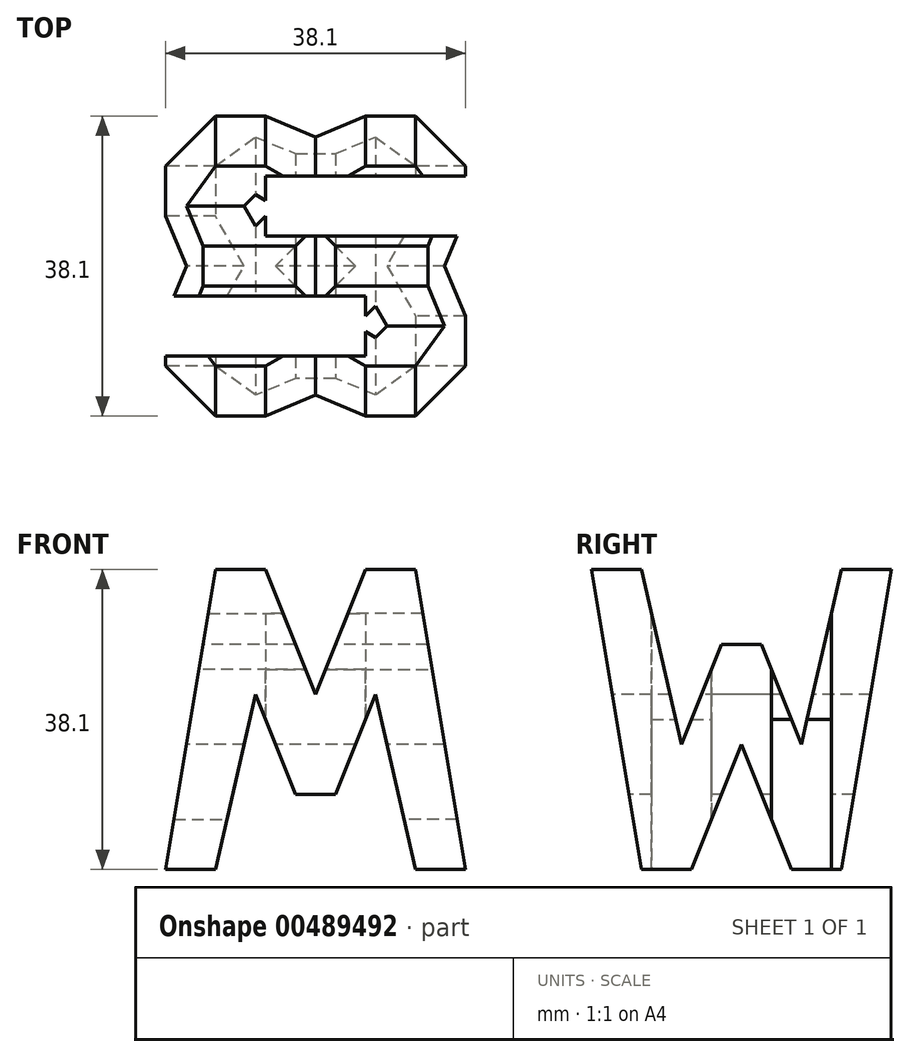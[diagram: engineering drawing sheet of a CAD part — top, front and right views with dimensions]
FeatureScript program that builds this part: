
annotation { "Feature Type Name" : "Feature", "Feature Type Description" : "" }
export const myFeature = defineFeature(function(context is Context, id is Id, definition is map)
    precondition{}
    {
        {
            var Q0;
            Q0=qCreatedBy(makeId("Front.planeOp"),FACE);
            var sketch = newSketch(context, id + "F0", { "sketchPlane" : qUnion([Q0])});
            skLineSegment(sketch, "E0", {"start": v(0, 0) * mm, "end": v(0, 38.1) * mm});
            skLineSegment(sketch, "E1", {"start": v(0, 38.1) * mm, "end": v(-38.1, 38.1) * mm});
            skLineSegment(sketch, "E2", {"start": v(-38.1, 38.1) * mm, "end": v(-38.1, 0) * mm});
            skLineSegment(sketch, "E3", {"start": v(-38.1, 0) * mm, "end": v(0, 0) * mm});
            skSolve(sketch);
        }
        {
            var Q0;
            Q0=makeQuery(id+"F0.imprint","IMPRINT",FACE,{"disambiguationData":[TD([[makeQuery(id+"F0.imprint","IMPRINT",EDGE,{"derivedFrom":sQuery(id+"F0.wireOp",EDGE,"E0")}),1.0]])]});
            extrude(context, id + "F1", {"entities" : qUnion([Q0]), "depth" : 38.1 * mm, "offsetDistance" : 25.4 * mm});
        }
        {
            var Q0;
            Q0=qCreatedBy(makeId("Front.planeOp"),FACE);
            cPlane(context, id + "F2", {"entities" : qUnion([Q0]), "cplaneType" : CPlaneType.OFFSET, "offset" : 38.1 * mm, "width" : 152.4 * mm, "height" : 152.4 * mm});
        }
        {
            var Q0;
            Q0=qCreatedBy(makeId("Right.planeOp"),FACE);
            cPlane(context, id + "F3", {"entities" : qUnion([Q0]), "cplaneType" : CPlaneType.OFFSET, "offset" : 38.1 * mm, "oppositeDirection" : true, "width" : 152.4 * mm, "height" : 152.4 * mm});
        }
        {
            var Q0;
            Q0=qCreatedBy(makeId("Top.planeOp"),FACE);
            cPlane(context, id + "F4", {"entities" : qUnion([Q0]), "cplaneType" : CPlaneType.OFFSET, "offset" : 38.1 * mm, "width" : 152.4 * mm, "height" : 152.4 * mm});
        }
        {
            var Q0;
            Q0=qCreatedBy(id+"F3.planeOp",FACE);
            var sketch = newSketch(context, id + "F5", { "sketchPlane" : qUnion([Q0])});
            skLineSegment(sketch, "E4", {"start": v(0, 38.1) * mm, "end": v(-38.1, 38.1) * mm});
            skLineSegment(sketch, "E5", {"start": v(-38.1, 38.1) * mm, "end": v(-38.1, 0) * mm});
            skLineSegment(sketch, "E6", {"start": v(0, 38.1) * mm, "end": v(-6.35, 0) * mm});
            skLineSegment(sketch, "E7", {"start": v(-6.35, 0) * mm, "end": v(-12.7, 0) * mm});
            skLineSegment(sketch, "E8", {"start": v(-12.7, 0) * mm, "end": v(-19.05, 15.88) * mm});
            skLineSegment(sketch, "E9", {"start": v(-19.05, 15.88) * mm, "end": v(-25.4, 0) * mm});
            skLineSegment(sketch, "E10", {"start": v(-25.4, 0) * mm, "end": v(-31.75, 0) * mm});
            skLineSegment(sketch, "E11", {"start": v(-31.75, 0) * mm, "end": v(-38.1, 38.1) * mm});
            skLineSegment(sketch, "E12", {"start": v(-31.75, 38.1) * mm, "end": v(-26.67, 15.88) * mm});
            skLineSegment(sketch, "E13", {"start": v(-26.67, 15.88) * mm, "end": v(-21.59, 28.58) * mm});
            skLineSegment(sketch, "E14", {"start": v(-21.6, 28.58) * mm, "end": v(-16.51, 28.58) * mm});
            skLineSegment(sketch, "E15", {"start": v(-16.51, 28.58) * mm, "end": v(-11.43, 15.88) * mm});
            skLineSegment(sketch, "E16", {"start": v(-11.43, 15.88) * mm, "end": v(-6.35, 38.1) * mm});
            skLineSegment(sketch, "E17", {"start": v(-6.35, 38.1) * mm, "end": v(0, 38.1) * mm});
            skLineSegment(sketch, "E18", {"start": v(0, 38.1) * mm, "end": v(0, 0) * mm});
            skLineSegment(sketch, "E19", {"start": v(0, 0) * mm, "end": v(-38.1, 0) * mm});
            skSolve(sketch);
        }
        {
            var Q0;
            {var subQ0=sQuery(id+"F5.wireOp",EDGE,"E12");Q0=makeQuery(id+"F5.imprint","IMPRINT",FACE,{"disambiguationData":[TD([[makeQuery(id+"F5.imprint","IMPRINT",EDGE,{"derivedFrom":subQ0}),1.0]])]});}
            var Q1;
            {var subQ0=sQuery(id+"F5.wireOp",EDGE,"E6");Q1=makeQuery(id+"F5.imprint","IMPRINT",FACE,{"disambiguationData":[TD([[makeQuery(id+"F5.imprint","IMPRINT",EDGE,{"derivedFrom":subQ0}),1.0]])]});}
            var Q2;
            {var subQ0=sQuery(id+"F5.wireOp",EDGE,"E8");Q2=makeQuery(id+"F5.imprint","IMPRINT",FACE,{"disambiguationData":[TD([[makeQuery(id+"F5.imprint","IMPRINT",EDGE,{"derivedFrom":subQ0}),1.0]])]});}
            var Q3;
            {var subQ0=sQuery(id+"F5.wireOp",EDGE,"E5");Q3=makeQuery(id+"F5.imprint","IMPRINT",FACE,{"disambiguationData":[TD([[makeQuery(id+"F5.imprint","IMPRINT",EDGE,{"derivedFrom":subQ0}),1.0]])]});}
            extrude(context, id + "F6", {"entities" : qUnion([Q0, Q1, Q2, Q3]), "operationType" : NewBodyOperationType.REMOVE, "depth" : 38.1 * mm, "offsetDistance" : 25.4 * mm});
        }
        {
            var Q0;
            Q0=qCreatedBy(id+"F2.planeOp",FACE);
            var sketch = newSketch(context, id + "F7", { "sketchPlane" : qUnion([Q0])});
            skLineSegment(sketch, "E20", {"start": v(-38.1, 38.1) * mm, "end": v(0, 38.1) * mm});
            skLineSegment(sketch, "E21", {"start": v(0, 38.1) * mm, "end": v(0, 0) * mm});
            skLineSegment(sketch, "E22", {"start": v(0, 0) * mm, "end": v(-38.1, 0) * mm});
            skLineSegment(sketch, "E23", {"start": v(-38.1, 0) * mm, "end": v(-38.1, 38.1) * mm});
            skLineSegment(sketch, "E24", {"start": v(-38.1, 0) * mm, "end": v(-31.75, 38.1) * mm});
            skLineSegment(sketch, "E25", {"start": v(-31.75, 38.1) * mm, "end": v(-25.4, 38.1) * mm});
            skLineSegment(sketch, "E26", {"start": v(-25.4, 38.1) * mm, "end": v(-19.05, 22.22) * mm});
            skLineSegment(sketch, "E27", {"start": v(-19.05, 22.22) * mm, "end": v(-12.7, 38.1) * mm});
            skLineSegment(sketch, "E28", {"start": v(-12.7, 38.1) * mm, "end": v(-6.35, 38.1) * mm});
            skLineSegment(sketch, "E29", {"start": v(-6.35, 38.1) * mm, "end": v(0, 0) * mm});
            skLineSegment(sketch, "E30", {"start": v(-6.35, 0) * mm, "end": v(-11.43, 22.22) * mm});
            skLineSegment(sketch, "E31", {"start": v(-11.43, 22.22) * mm, "end": v(-16.5, 9.52) * mm});
            skLineSegment(sketch, "E32", {"start": v(-16.5, 9.52) * mm, "end": v(-21.59, 9.52) * mm});
            skLineSegment(sketch, "E33", {"start": v(-21.59, 9.52) * mm, "end": v(-26.67, 22.22) * mm});
            skLineSegment(sketch, "E34", {"start": v(-26.67, 22.22) * mm, "end": v(-31.75, 0) * mm});
            skLineSegment(sketch, "E35", {"start": v(-31.75, 0) * mm, "end": v(-38.1, 0) * mm});
            skSolve(sketch);
        }
        {
            var Q0;
            {var subQ0=sQuery(id+"F7.wireOp",EDGE,"E30");Q0=makeQuery(id+"F7.imprint","IMPRINT",FACE,{"disambiguationData":[TD([[makeQuery(id+"F7.imprint","IMPRINT",EDGE,{"derivedFrom":subQ0}),1.0]])]});}
            var Q1;
            {var subQ0=sQuery(id+"F7.wireOp",EDGE,"E23");Q1=makeQuery(id+"F7.imprint","IMPRINT",FACE,{"disambiguationData":[TD([[makeQuery(id+"F7.imprint","IMPRINT",EDGE,{"derivedFrom":subQ0}),-1.0]])]});}
            var Q2;
            {var subQ0=sQuery(id+"F7.wireOp",EDGE,"E26");Q2=makeQuery(id+"F7.imprint","IMPRINT",FACE,{"disambiguationData":[TD([[makeQuery(id+"F7.imprint","IMPRINT",EDGE,{"derivedFrom":subQ0}),1.0]])]});}
            var Q3;
            {var subQ0=sQuery(id+"F7.wireOp",EDGE,"E21");Q3=makeQuery(id+"F7.imprint","IMPRINT",FACE,{"disambiguationData":[TD([[makeQuery(id+"F7.imprint","IMPRINT",EDGE,{"derivedFrom":subQ0}),-1.0]])]});}
            extrude(context, id + "F8", {"entities" : qUnion([Q0, Q1, Q2, Q3]), "operationType" : NewBodyOperationType.REMOVE, "oppositeDirection" : true, "depth" : 38.1 * mm, "offsetDistance" : 25.4 * mm});
        }
        {
            var Q0;
            Q0=qCreatedBy(id+"F4.planeOp",FACE);
            var sketch = newSketch(context, id + "F9", { "sketchPlane" : qUnion([Q0])});
            skLineSegment(sketch, "E36", {"start": v(0, 0) * mm, "end": v(0, -38.1) * mm});
            skLineSegment(sketch, "E37", {"start": v(0, -38.1) * mm, "end": v(-38.1, -38.1) * mm});
            skLineSegment(sketch, "E38", {"start": v(-38.1, -38.1) * mm, "end": v(-38.1, 0) * mm});
            skLineSegment(sketch, "E39", {"start": v(-38.1, 0) * mm, "end": v(0, 0) * mm});
            skLineSegment(sketch, "E40", {"start": v(0, -7.62) * mm, "end": v(-25.4, -7.62) * mm});
            skLineSegment(sketch, "E41", {"start": v(-25.4, -7.62) * mm, "end": v(-25.4, -15.24) * mm});
            skLineSegment(sketch, "E42", {"start": v(-25.4, -15.24) * mm, "end": v(0, -15.24) * mm});
            skLineSegment(sketch, "E43", {"start": v(-38.1, -30.48) * mm, "end": v(-12.7, -30.48) * mm});
            skLineSegment(sketch, "E44", {"start": v(-12.7, -30.48) * mm, "end": v(-12.7, -22.86) * mm});
            skLineSegment(sketch, "E45", {"start": v(-12.7, -22.86) * mm, "end": v(-38.1, -22.86) * mm});
            skSolve(sketch);
        }
        {
            var Q0;
            {var subQ0=sQuery(id+"F9.wireOp",EDGE,"E40");Q0=makeQuery(id+"F9.imprint","IMPRINT",FACE,{"disambiguationData":[TD([[makeQuery(id+"F9.imprint","IMPRINT",EDGE,{"derivedFrom":subQ0}),1.0]])]});}
            var Q1;
            {var subQ0=sQuery(id+"F9.wireOp",EDGE,"E43");Q1=makeQuery(id+"F9.imprint","IMPRINT",FACE,{"disambiguationData":[TD([[makeQuery(id+"F9.imprint","IMPRINT",EDGE,{"derivedFrom":subQ0}),1.0]])]});}
            extrude(context, id + "F10", {"entities" : qUnion([Q0, Q1]), "operationType" : NewBodyOperationType.REMOVE, "oppositeDirection" : true, "depth" : 38.1 * mm, "offsetDistance" : 25.4 * mm});
        }
    });
